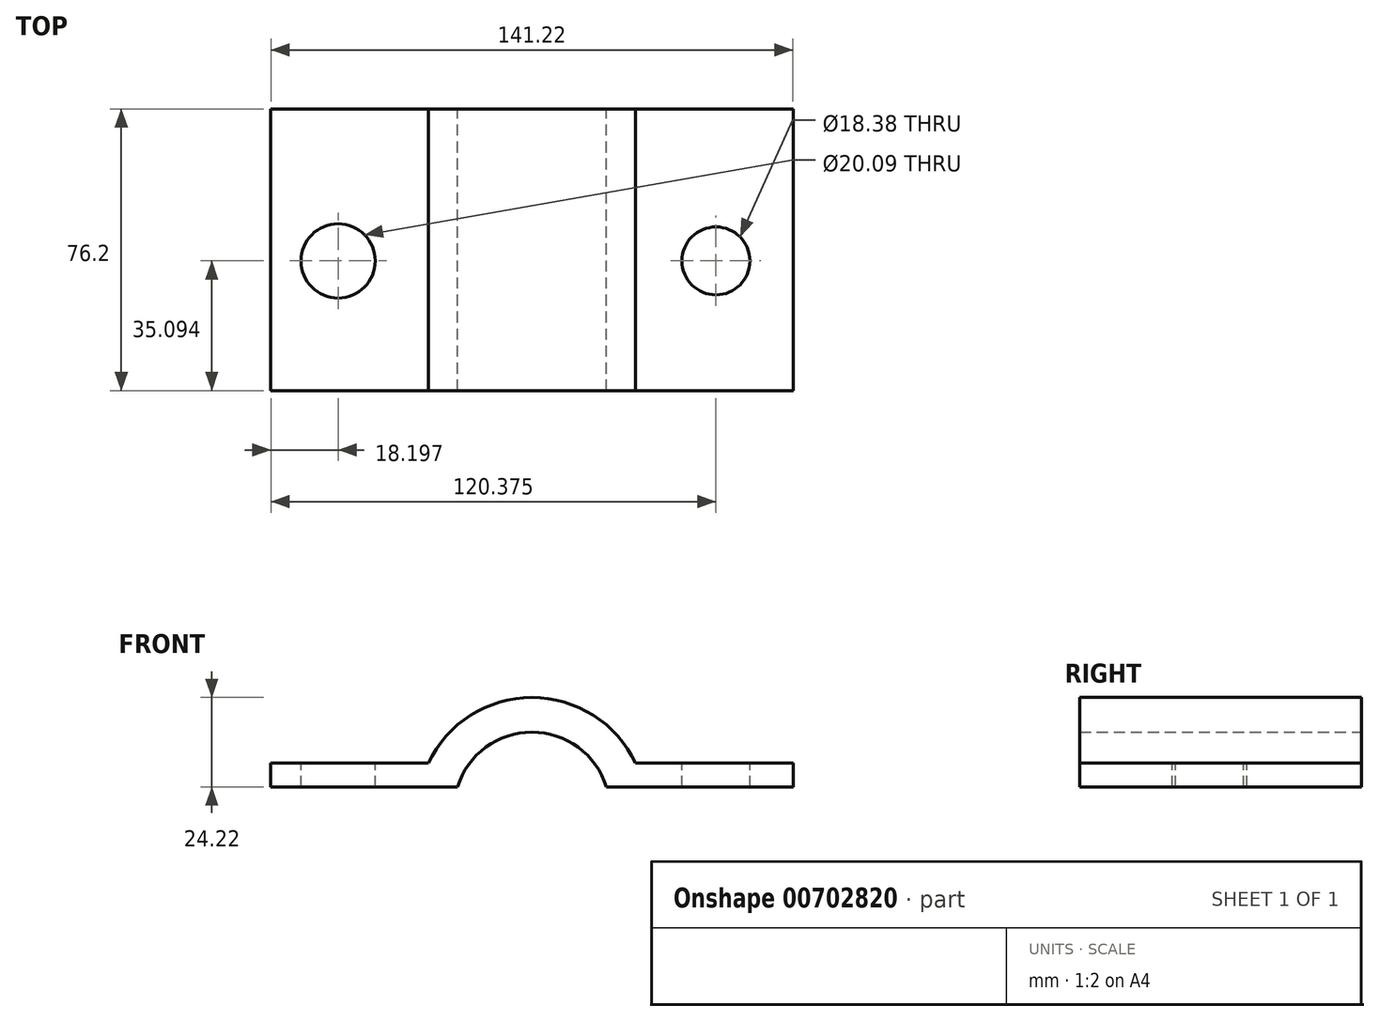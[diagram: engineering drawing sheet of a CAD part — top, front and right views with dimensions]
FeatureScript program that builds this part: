
annotation { "Feature Type Name" : "Feature", "Feature Type Description" : "" }
export const myFeature = defineFeature(function(context is Context, id is Id, definition is map)
    precondition{}
    {
        {
            var Q0;
            Q0=qCreatedBy(makeId("Front.planeOp"),FACE);
            var sketch = newSketch(context, id + "F0", { "sketchPlane" : qUnion([Q0])});
            skLineSegment(sketch, "E0", {"start": v(-63.27, 10.57) * mm, "end": v(-12.77, 10.57) * mm});
            skLineSegment(sketch, "E1", {"start": v(-63.27, 10.57) * mm, "end": v(-63.27, 17.03) * mm});
            skLineSegment(sketch, "E2", {"start": v(-63.27, 17.03) * mm, "end": v(-20.7, 17.03) * mm});
            skLineSegment(sketch, "E3", {"start": v(27.45, 10.57) * mm, "end": v(77.95, 10.57) * mm});
            skLineSegment(sketch, "E4", {"start": v(77.95, 10.57) * mm, "end": v(77.95, 17.03) * mm});
            skPoint(sketch, "E4.endSnap0", {"position": v(-41.99, 17.03) * mm});
            skLineSegment(sketch, "E5", {"start": v(77.95, 17.03) * mm, "end": v(35.38, 17.03) * mm});
            skArc(sketch, "E6", {"start": v(35.38, 17.03) * mm, "mid": v(7.34, 34.8) * mm, "end": v(-20.7, 17.03) * mm});
            skArc(sketch, "E7", {"start": v(27.45, 10.57) * mm, "mid": v(7.34, 25.42) * mm, "end": v(-12.77, 10.57) * mm});
            skSolve(sketch);
        }
        {
            var Q0;
            Q0 = qSketchRegion(id + "F0", true);
            extrude(context, id + "F1", {"entities" : qUnion([Q0]), "depth" : 76.2 * mm, "offsetDistance" : 25.4 * mm});
        }
        {
            var Q0;
            Q0=makeQuery(id+"F1.opExtrude","SWEPT_FACE",FACE,{"disambiguationData":[OSD([sQuery(id+"F0.wireOp",EDGE,"E2")])]});
            var sketch = newSketch(context, id + "F2", { "sketchPlane" : qUnion([Q0])});
            skCircle(sketch, "E8", {"center": v(-45.07, -41.1) * mm, "radius": 10.04 * mm});
            skCircle(sketch, "E9", {"center": v(57.1, -41.1) * mm, "radius": 9.2 * mm});
            skSolve(sketch);
        }
        {
            var Q0;
            Q0 = qSketchRegion(id + "F2", true);
            extrude(context, id + "F3", {"entities" : qUnion([Q0]), "operationType" : NewBodyOperationType.REMOVE, "oppositeDirection" : true, "depth" : 25.4 * mm, "offsetDistance" : 25.4 * mm});
        }
    });
